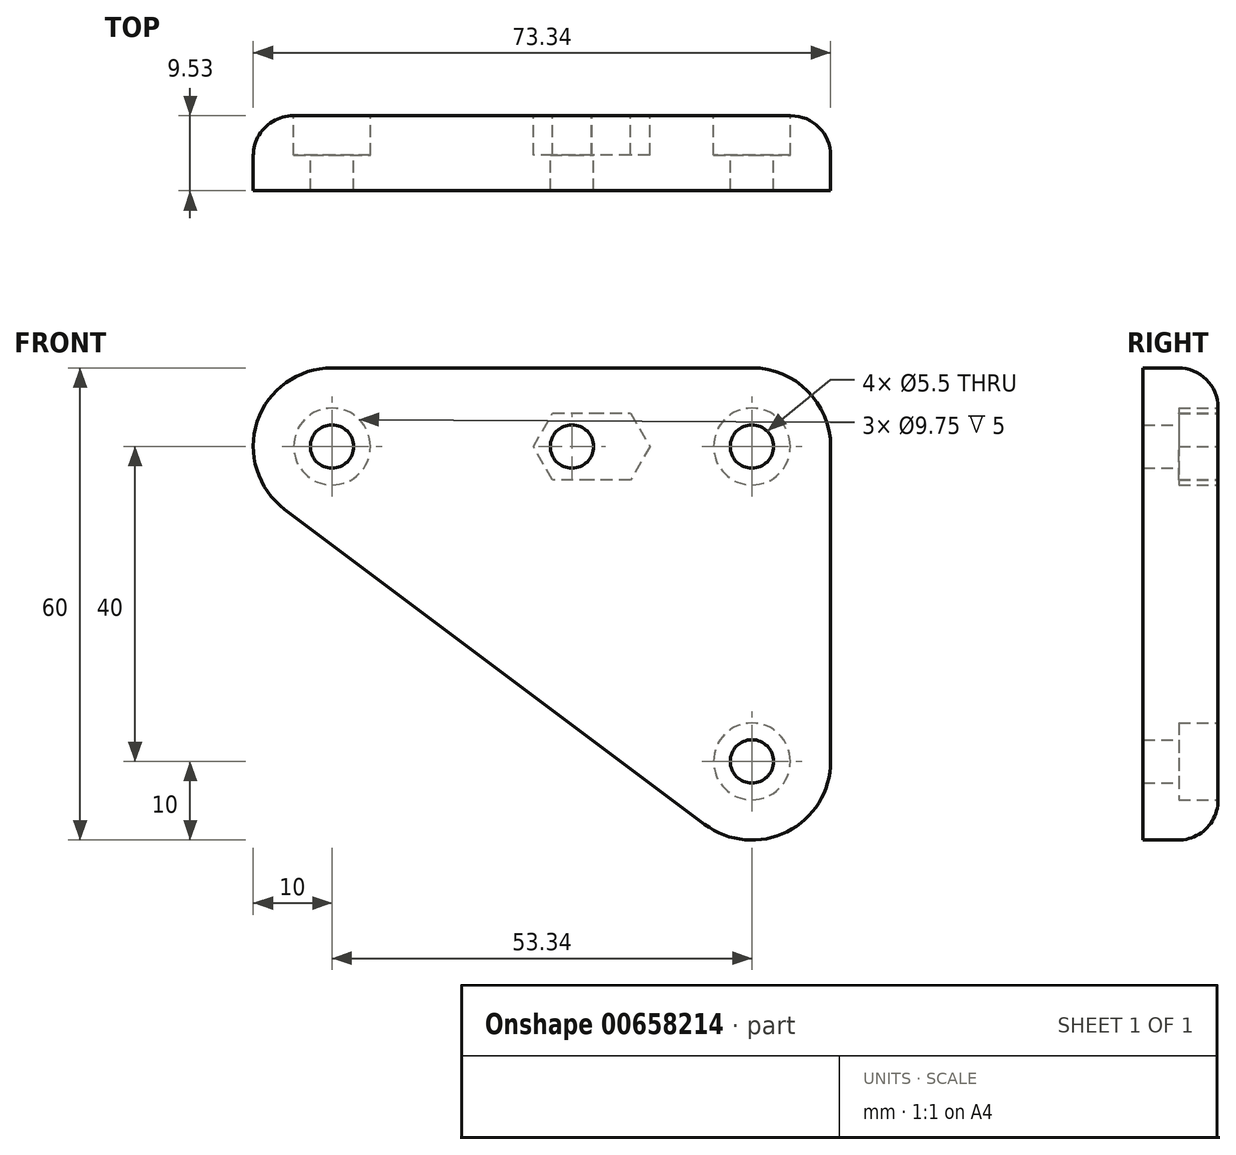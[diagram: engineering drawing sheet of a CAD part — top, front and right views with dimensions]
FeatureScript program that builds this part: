
annotation { "Feature Type Name" : "Feature", "Feature Type Description" : "" }
export const myFeature = defineFeature(function(context is Context, id is Id, definition is map)
    precondition{}
    {
        {
            var Q0;
            Q0=qCreatedBy(makeId("Front.planeOp"),FACE);
            var sketch = newSketch(context, id + "F0", { "sketchPlane" : qUnion([Q0])});
            skPoint(sketch, "E0", {"position": v(-22.86, 0) * mm});
            skArc(sketch, "E1", {"start": v(10, 0) * mm, "mid": v(7.07, 7.07) * mm, "end": v(0, 10) * mm});
            skPoint(sketch, "E2", {"position": v(0, -40) * mm});
            skArc(sketch, "E3", {"start": v(-6, -48) * mm, "mid": v(4.47, -48.94) * mm, "end": v(10, -40) * mm});
            skArc(sketch, "E4", {"start": v(-53.34, 10) * mm, "mid": v(-62.83, 3.16) * mm, "end": v(-59.34, -8) * mm});
            skLineSegment(sketch, "E5", {"start": v(-59.34, -8) * mm, "end": v(-6, -48) * mm});
            skLineSegment(sketch, "E6", {"start": v(-53.34, 10) * mm, "end": v(0, 10) * mm});
            skLineSegment(sketch, "E7", {"start": v(10, -40) * mm, "end": v(10, 0) * mm});
            skCircle(sketch, "E8.cCircle", {"center": v(-22.86, 0) * mm, "radius": 4.25 * mm, "construction": true});
            skLineSegment(sketch, "E8.0", {"start": v(-20.4, -4.25) * mm, "end": v(-25.31, -4.25) * mm});
            skLineSegment(sketch, "E8.1", {"start": v(-25.31, -4.25) * mm, "end": v(-27.77, 0) * mm});
            skLineSegment(sketch, "E8.2", {"start": v(-27.77, 0) * mm, "end": v(-25.31, 4.25) * mm});
            skLineSegment(sketch, "E8.3", {"start": v(-25.31, 4.25) * mm, "end": v(-20.4, 4.25) * mm});
            skLineSegment(sketch, "E8.4", {"start": v(-20.4, 4.25) * mm, "end": v(-17.95, 0) * mm});
            skLineSegment(sketch, "E8.5", {"start": v(-17.95, 0) * mm, "end": v(-20.4, -4.25) * mm});
            skPoint(sketch, "E8.0.midPoint", {"position": v(-22.86, -4.25) * mm});
            skLineSegment(sketch, "E9.1.0.0", {"start": v(-15.4, 4.25) * mm, "end": v(-12.95, 0) * mm});
            skLineSegment(sketch, "E9.1.0.1", {"start": v(-20.31, 4.25) * mm, "end": v(-15.4, 4.25) * mm});
            skLineSegment(sketch, "E9.1.0.2", {"start": v(-22.77, 0) * mm, "end": v(-20.31, 4.25) * mm});
            skLineSegment(sketch, "E9.1.0.3", {"start": v(-20.31, -4.25) * mm, "end": v(-22.77, 0) * mm});
            skLineSegment(sketch, "E9.1.0.4", {"start": v(-15.4, -4.25) * mm, "end": v(-20.31, -4.25) * mm});
            skLineSegment(sketch, "E9.1.0.5", {"start": v(-12.95, 0) * mm, "end": v(-15.4, -4.25) * mm});
            skLineSegment(sketch, "E9.direction1", {"start": v(-17.95, 0) * mm, "end": v(-12.95, 0) * mm, "construction": true});
            skSolve(sketch);
        }
        {
            var Q0;
            Q0=makeQuery(id+"F0.imprint","IMPRINT",FACE,{"disambiguationData":[TD([[makeQuery(id+"F0.imprint","IMPRINT",EDGE,{"derivedFrom":sQuery(id+"F0.wireOp",EDGE,"E1")}),1.0]])]});
            var Q1;
            {var subQ6=sQuery(id+"F0.wireOp",EDGE,"E8.0");Q1=makeQuery(id+"F0.imprint","IMPRINT",FACE,{"disambiguationData":[TD([[makeQuery(id+"F0.imprint","IMPRINT",EDGE,{"derivedFrom":subQ6}),-1.0]])]});}
            var Q2;
            Q2=makeQuery(id+"F0.imprint","IMPRINT",FACE,{"disambiguationData":[TD([[makeQuery(id+"F0.imprint","IMPRINT",EDGE,{"derivedFrom":sQuery(id+"F0.wireOp",EDGE,"E9.1.0.0")}),-1.0]])]});
            var Q3;
            {var subQ0=sQuery(id+"F0.wireOp",EDGE,"E8.5");var subQ1=sQuery(id+"F0.wireOp",EDGE,"E8.4");var subQ2=makeQuery(id+"F0.imprint","INTERSECT",VERTEX,{"derivedFrom":[subQ1,subQ0]});Q3=makeQuery(id+"F0.imprint","IMPRINT",FACE,{"disambiguationData":[TD([[makeQuery(id+"F0.imprint","IMPRINT",EDGE,{"disambiguationData":[TD([[subQ2,1.0]])],"derivedFrom":subQ1}),-1.0]])]});}
            extrude(context, id + "F1", {"entities" : qUnion([Q0, Q1, Q2, Q3]), "depth" : 9.52 * mm, "offsetDistance" : 25.4 * mm});
        }
        {
            var Q0;
            Q0=sQuery(id+"F0.wireOp",VERTEX,"E1.center");
            var Q1;
            Q1=sQuery(id+"F0.wireOp",VERTEX,"E2");
            var Q2;
            Q2=sQuery(id+"F0.wireOp",VERTEX,"f07db37f-82a6-4f9c-b0d2-fdbc7351bc77.MirrorP");
            var Q3;
            Q3=sQuery(id+"F0.wireOp",VERTEX,"E4.center");
            var Q4;
            Q4=makeQuery(id+"F1.opExtrude","SWEPT_BODY",BODY,{"disambiguationData":[OSD([sQuery(id+"F0.wireOp",EDGE,"bf2f238d-4e1d-4e86-ab75-1465cd813df2.MirrorCS"),sQuery(id+"F0.wireOp",EDGE,"7d5bedbb-471c-4160-8e68-eb1f4d767648.MirrorCS"),sQuery(id+"F0.wireOp",EDGE,"bc7fee83-9e46-4c51-805a-8ae9689402aa.MirrorCS"),sQuery(id+"F0.wireOp",EDGE,"e5d497b7-cccf-4703-a1dc-18e520bbeae9.MirrorCS"),sQuery(id+"F0.wireOp",EDGE,"c155fd9a-5cc5-4759-a1c6-071fd15af197.MirrorCS"),sQuery(id+"F0.wireOp",EDGE,"33a989d6-5cc4-4172-ab73-ca817da9f412.MirrorCS"),sQuery(id+"F0.wireOp",EDGE,"1c3aec17-fec7-453e-8acd-3df81b9bc4e3.MirrorCS"),sQuery(id+"F0.wireOp",EDGE,"0cd19f4d-6d86-4b4a-a093-bb589b475590.MirrorCS"),sQuery(id+"F0.wireOp",EDGE,"eee5d6f5-912f-4719-99ba-1d72e724f1e9.MirrorCS"),sQuery(id+"F0.wireOp",EDGE,"64a401ff-d109-42b1-96b9-6f7f2e519c4d.MirrorCS"),sQuery(id+"F0.wireOp",EDGE,"2bc110f3-ae92-45de-b2b7-7df43831b8ab"),sQuery(id+"F0.wireOp",EDGE,"pibmvETk-c1Xj-BIgN-8uma-1jo4IxxjolSW")])]});
            var Q5;
            Q5=makeQuery(id+"F1.opExtrude","SWEPT_BODY",BODY,{"disambiguationData":[OSD([sQuery(id+"F0.wireOp",EDGE,"E1"),sQuery(id+"F0.wireOp",EDGE,"E3"),sQuery(id+"F0.wireOp",EDGE,"E4"),sQuery(id+"F0.wireOp",EDGE,"E5"),sQuery(id+"F0.wireOp",EDGE,"E6"),sQuery(id+"F0.wireOp",EDGE,"E7"),sQuery(id+"F0.wireOp",EDGE,"abe57e29-0c7c-4b99-905f-2de660d06fb5.0"),sQuery(id+"F0.wireOp",EDGE,"3414c082-77eb-4b60-8568-4fb26c363dc8.0"),sQuery(id+"F0.wireOp",EDGE,"de1da2a2-a23f-4f41-af84-cb727b929bf4.0"),sQuery(id+"F0.wireOp",EDGE,"a5e2c965-bc7c-4ac8-a8c3-57b03be74d22.filletArc"),sQuery(id+"F0.wireOp",EDGE,"b6b388fa-fd1b-47d1-968e-da1be4f55a76.filletArc"),sQuery(id+"F0.wireOp",EDGE,"61007793-95a0-45a8-9965-7a1efe876f03.filletArc")])]});
            hole(context, id + "F2", {"style" : HoleStyle.C_BORE, "endStyle" : HoleEndStyle.THROUGH, "oppositeDirection" : true, "standardTappedOrClearance" : lookupTablePath({ "standard" : "ISO", "fit" : "Normal", "size" : "M5", "type" : "Clearance" }), "standardBlindInLast" : lookupTablePath({ "fit" : "Standard", "standard" : "ISO", "size" : "M5", "type" : "Clearance" }), "holeDiameter" : 5.5 * mm, "cBoreDiameter" : 9.75 * mm, "cBoreDepth" : 5 * mm, "majorDiameter" : 6.35 * mm, "isTappedThrough" : true, "tappedDepth" : 12.7 * mm, "tapClearance" : 3, "locations" : qUnion([Q0, Q1, Q2, Q3]), "scope" : qUnion([Q4, Q5])});
        }
        {
            var Q0;
            Q0=makeQuery(id+"F1.opExtrude","CAP_EDGE",EDGE,{"disambiguationData":[OSD([sQuery(id+"F0.wireOp",EDGE,"E6")])],"isStart":true});
            var Q1;
            Q1=makeQuery(id+"F1.opExtrude","CAP_EDGE",EDGE,{"disambiguationData":[OSD([sQuery(id+"F0.wireOp",EDGE,"de1da2a2-a23f-4f41-af84-cb727b929bf4.0")])],"isStart":true});
            fillet(context, id + "F3", {"entities" : qUnion([Q0, Q1]), "radius" : 5.08 * mm, "tangentPropagation" : true, "allowEdgeOverflow" : false});
        }
        {
            var Q0;
            Q0=makeQuery(id+"F0.imprint","IMPRINT",FACE,{"disambiguationData":[TD([[makeQuery(id+"F0.imprint","IMPRINT",EDGE,{"derivedFrom":sQuery(id+"F0.wireOp",EDGE,"E8.0")}),-1.0]])]});
            var Q1;
            {var subQ0=sQuery(id+"F0.wireOp",EDGE,"E8.5");var subQ1=sQuery(id+"F0.wireOp",EDGE,"E8.4");var subQ2=makeQuery(id+"F0.imprint","INTERSECT",VERTEX,{"derivedFrom":[subQ1,subQ0]});Q1=makeQuery(id+"F0.imprint","IMPRINT",FACE,{"disambiguationData":[TD([[makeQuery(id+"F0.imprint","IMPRINT",EDGE,{"disambiguationData":[TD([[subQ2,1.0]])],"derivedFrom":subQ1}),-1.0]])]});}
            var Q2;
            Q2=makeQuery(id+"F0.imprint","IMPRINT",FACE,{"disambiguationData":[TD([[makeQuery(id+"F0.imprint","IMPRINT",EDGE,{"derivedFrom":sQuery(id+"F0.wireOp",EDGE,"E9.1.0.0")}),-1.0]])]});
            extrude(context, id + "F4", {"entities" : qUnion([Q0, Q1, Q2]), "operationType" : NewBodyOperationType.REMOVE, "depth" : 5 * mm, "offsetDistance" : 25.4 * mm});
        }
        {
            var Q0;
            Q0=sQuery(id+"F0.wireOp",VERTEX,"E0");
            var Q1;
            Q1=sQuery(id+"F0.wireOp",VERTEX,"c6682d48-5f0b-4c8b-bbf4-16eb70b1295b");
            var Q2;
            Q2=sQuery(id+"F0.wireOp",VERTEX,"ef7b1b70-f73b-4085-9232-99095e9cd9a3");
            var Q3;
            Q3=makeQuery(id+"F1.opExtrude","SWEPT_BODY",BODY,{"disambiguationData":[OSD([sQuery(id+"F0.wireOp",EDGE,"E1"),sQuery(id+"F0.wireOp",EDGE,"E3"),sQuery(id+"F0.wireOp",EDGE,"E4"),sQuery(id+"F0.wireOp",EDGE,"E5"),sQuery(id+"F0.wireOp",EDGE,"E6"),sQuery(id+"F0.wireOp",EDGE,"E7")])]});
            hole(context, id + "F5", {"style" : HoleStyle.SIMPLE, "endStyle" : HoleEndStyle.THROUGH, "oppositeDirection" : true, "standardTappedOrClearance" : lookupTablePath({ "standard" : "ISO", "fit" : "Normal", "size" : "M5", "type" : "Clearance" }), "standardBlindInLast" : lookupTablePath({ "fit" : "Standard", "standard" : "ISO", "size" : "M5", "type" : "Clearance" }), "holeDiameter" : 5.5 * mm, "majorDiameter" : 6.35 * mm, "isTappedThrough" : true, "tappedDepth" : 12.7 * mm, "tapClearance" : 3, "locations" : qUnion([Q0, Q1, Q2]), "scope" : qUnion([Q3])});
        }
    });
